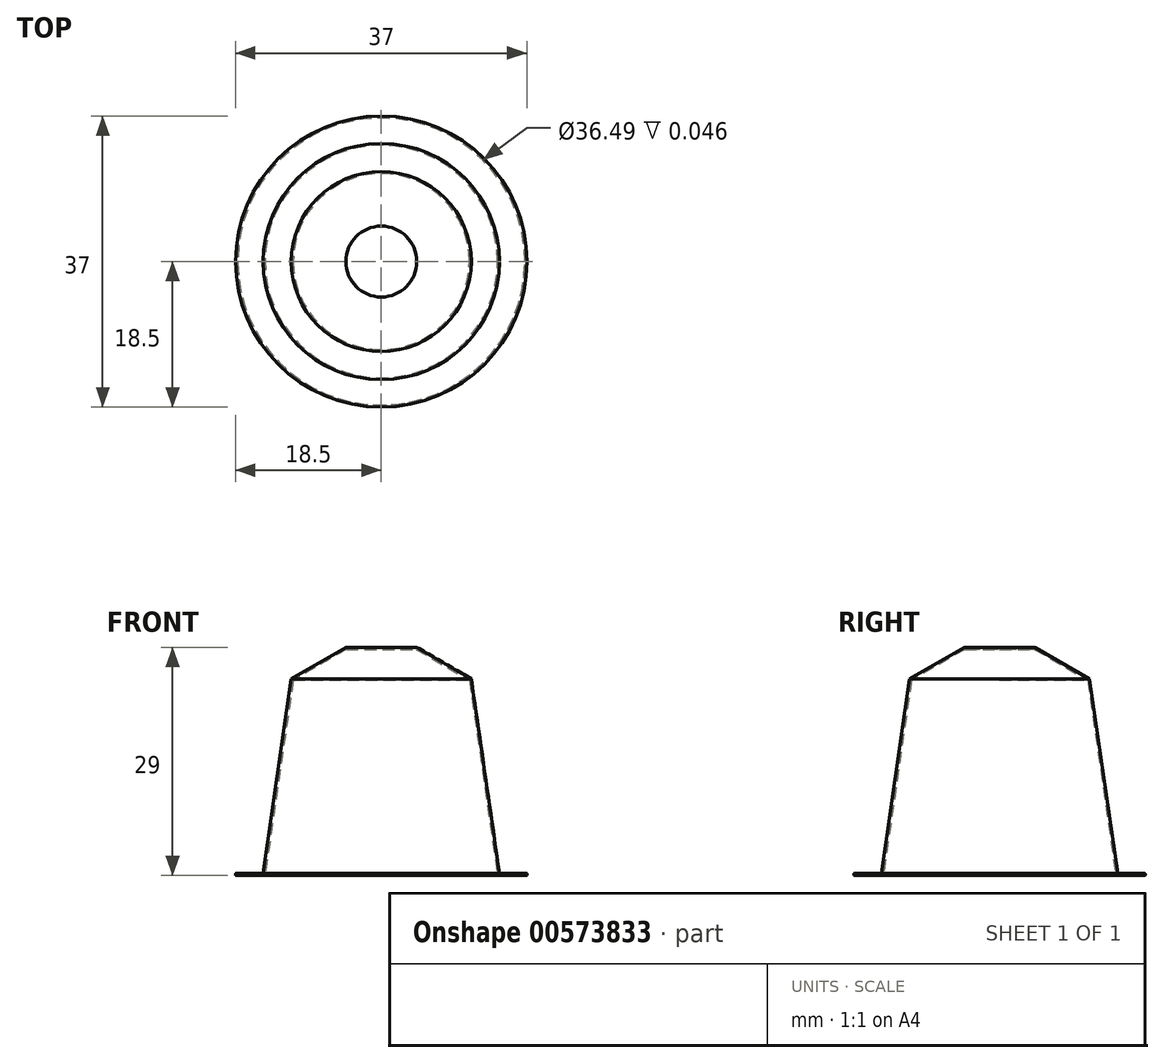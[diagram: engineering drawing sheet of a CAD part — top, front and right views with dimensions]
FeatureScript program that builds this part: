
annotation { "Feature Type Name" : "Feature", "Feature Type Description" : "" }
export const myFeature = defineFeature(function(context is Context, id is Id, definition is map)
    precondition{}
    {
        {
            var Q0;
            Q0=qCreatedBy(makeId("Front.planeOp"),FACE);
            var sketch = newSketch(context, id + "F0", { "sketchPlane" : qUnion([Q0])});
            skLineSegment(sketch, "E0", {"start": v(0, 0) * mm, "end": v(-18.5, 0) * mm});
            skLineSegment(sketch, "E1", {"start": v(-18.5, 0) * mm, "end": v(-18.5, 0.3) * mm});
            skLineSegment(sketch, "E2", {"start": v(-18.5, 0.3) * mm, "end": v(-15, 0.3) * mm});
            skLineSegment(sketch, "E3", {"start": v(-15, 0.3) * mm, "end": v(-11.43, 25) * mm});
            skLineSegment(sketch, "E4", {"start": v(-11.43, 25) * mm, "end": v(-4.5, 29) * mm});
            skLineSegment(sketch, "E5", {"start": v(-4.5, 29) * mm, "end": v(0, 29) * mm});
            skLineSegment(sketch, "E6", {"start": v(0, 29) * mm, "end": v(0, 0) * mm});
            skSolve(sketch);
        }
        {
            var Q0;
            Q0 = qSketchRegion(id + "F0", true);
            var Q1;
            Q1=sQuery(id+"F0.wireOp",EDGE,"E6");
            revolve(context, id + "F1", {"entities" : qUnion([Q0]), "axis" : qUnion([Q1]), "revolveType" : RevolveType.FULL});
        }
        {
            var Q0;
            Q0=makeQuery(id+"F1.opRevolve","SWEPT_EDGE",EDGE,{"disambiguationData":[OSD([sQuery(id+"F0.wireOp",EDGE,"E0"),sQuery(id+"F0.wireOp",EDGE,"E1")])]});
            var Q1;
            Q1=makeQuery(id+"F1.opRevolve","SWEPT_EDGE",EDGE,{"disambiguationData":[OSD([sQuery(id+"F0.wireOp",EDGE,"E1"),sQuery(id+"F0.wireOp",EDGE,"E2")])]});
            fillet(context, id + "F2", {"entities" : qUnion([Q0, Q1]), "radius" : 0.1 * mm, "tangentPropagation" : true, "allowEdgeOverflow" : false});
        }
        {
            var Q0;
            Q0=makeQuery(id+"F1.opRevolve","SWEPT_FACE",FACE,{"disambiguationData":[OSD([sQuery(id+"F0.wireOp",EDGE,"E0")])]});
            shell(context, id + "F3", {"entities" : qUnion([Q0]), "thickness" : 0.25 * mm});
        }
    });
